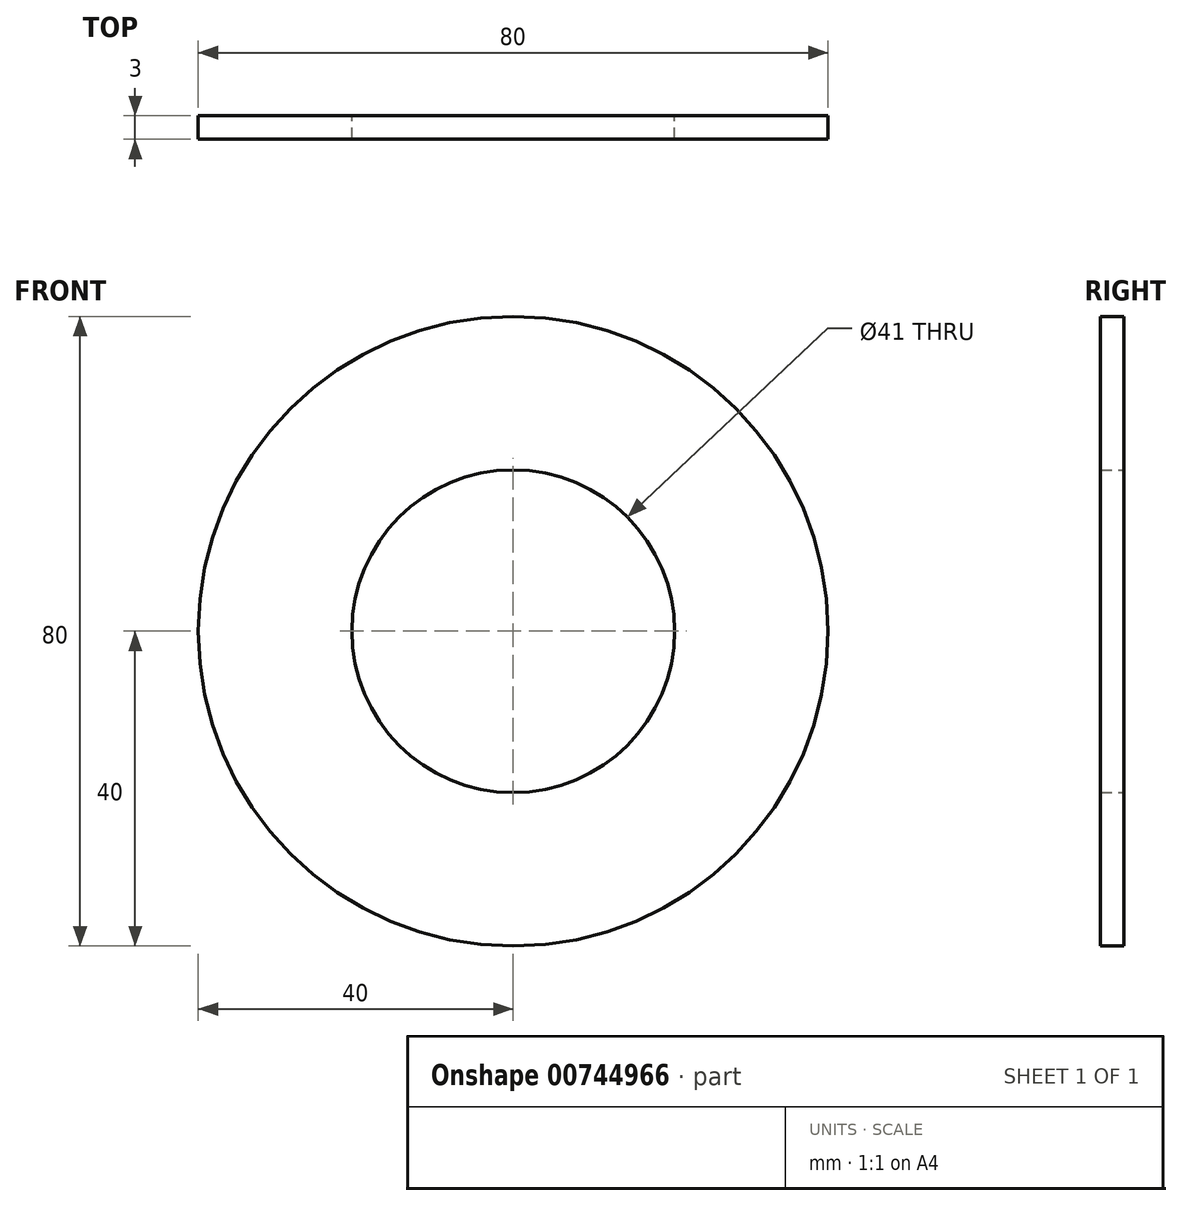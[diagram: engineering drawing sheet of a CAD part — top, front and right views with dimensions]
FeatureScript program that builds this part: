
annotation { "Feature Type Name" : "Feature", "Feature Type Description" : "" }
export const myFeature = defineFeature(function(context is Context, id is Id, definition is map)
    precondition{}
    {
        {
            var Q0;
            Q0=qCreatedBy(makeId("Front.planeOp"),FACE);
            var sketch = newSketch(context, id + "F0", { "sketchPlane" : qUnion([Q0])});
            skCircle(sketch, "E0", {"center": v(0, 0) * mm, "radius": 20.5 * mm});
            skCircle(sketch, "E1", {"center": v(0, 0) * mm, "radius": 40 * mm});
            skSolve(sketch);
        }
        {
            var Q0;
            Q0 = qSketchRegion(id + "F0", true);
            extrude(context, id + "F1", {"entities" : qUnion([Q0]), "depth" : 3 * mm, "offsetDistance" : 25 * mm});
        }
    });
